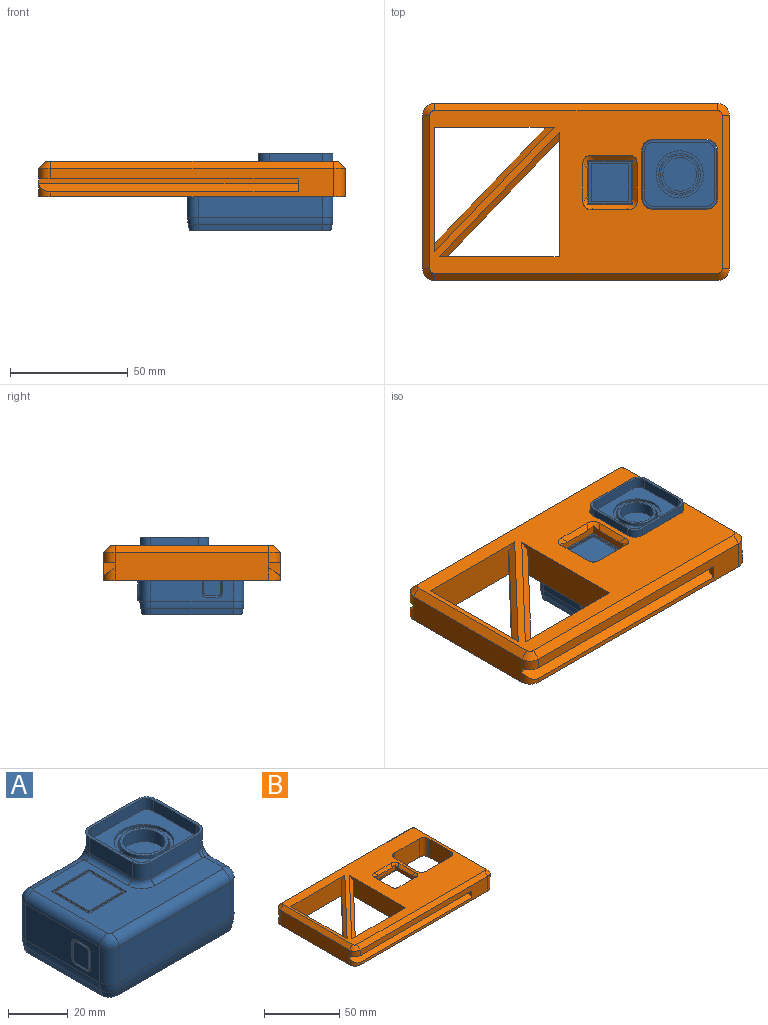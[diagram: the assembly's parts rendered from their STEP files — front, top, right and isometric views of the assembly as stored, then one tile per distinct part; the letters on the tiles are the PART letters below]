
ASSEMBLY  parts=2 mates=1
PART A: 128 faces, bbox 66x48.4x32.7 mm
  f0: plane 35.1x14.78mm, normal (-1,0,0), area 431.7mm2, adj f6,f7,f25,f94,f120,f121,f122,f123
  f1: plane 35.1x27.03mm, normal (1,0,0), area 775.9mm2, adj f4,f5,f9,f14,f20,f21,f102
  f2: plane 52.7x27.03mm, normal (0,1,0), area 881.6mm2, adj f5,f6,f10,f14,f27,f28,f57,f58
  f3: plane 52.7x14.78mm, normal (0,-1,0), area 779.1mm2, adj f4,f7,f23,f98
  f4: cylinder r=4.5mm len=14.78mm, axis (0,0,1), area 104.5mm2, adj f1,f3,f22,f100
  f5: cylinder r=4.5mm len=27.03mm, axis (0,0,1), area 191.1mm2, adj f1,f2,f14,f101
  f6: cylinder r=4.5mm len=14.78mm, axis (0,0,1), area 104.5mm2, adj f0,f2,f26,f92
  f7: cylinder r=4.5mm len=14.78mm, axis (0,0,1), area 104.5mm2, adj f0,f3,f24,f96
  f8: plane 54.3x36.7mm, normal (0,0,1), area 852.6mm2, adj f15,f16,f17,f18,f19,f21,f22,f23
  f9: cylinder r=4.5mm len=6.45mm, axis (0,0,-1), area 45.6mm2, adj f1,f13,f14,f15
  f10: cylinder r=4.5mm len=6.45mm, axis (0,0,-1), area 45.6mm2, adj f2,f11,f14,f19
  f11: plane 20.15x6.45mm, normal (-1,0,0), area 130mm2, adj f10,f12,f14,f18
  f12: cylinder r=4.5mm len=6.45mm, axis (0,0,-1), area 45.6mm2, adj f11,f13,f14,f17
  f13: plane 22.55x6.45mm, normal (0,-1,0), area 145.4mm2, adj f9,f12,f14,f16
  f14: plane 31.55x29.15mm, normal (0,0,1), area 110.5mm2, adj f1,f2,f5,f9,f10,f11,f12,f13
  f15: torus R=6.6mm, axis (0,0,1), area 7.9mm2, adj f8,f9,f16,f20
  f16: cylinder r=2.1mm len=22.55mm, axis (1,0,0), area 74.4mm2, adj f8,f13,f15,f17
  f17: torus R=6.6mm, axis (0,0,1), area 27.3mm2, adj f8,f12,f16,f18
  f18: cylinder r=2.1mm len=20.15mm, axis (0,-1,0), area 66.5mm2, adj f8,f11,f17,f19
  f19: torus R=6.6mm, axis (0,0,1), area 7.9mm2, adj f8,f10,f18,f28
  f20: bspline ~7.66x5.8mm, area 27.6mm2, adj f1,f15,f21
  f21: cylinder r=3.7mm len=8.4mm, axis (0,1,0), area 48.8mm2, adj f1,f8,f20,f22
  f22: torus R=0.8mm, axis (0,0,1), area 28.8mm2, adj f4,f8,f21,f23
  f23: cylinder r=3.7mm len=52.7mm, axis (1,0,0), area 306.3mm2, adj f3,f8,f22,f24
  f24: torus R=0.8mm, axis (0,0,1), area 28.8mm2, adj f7,f8,f23,f25
  f25: cylinder r=3.7mm len=35.1mm, axis (0,-1,0), area 204mm2, adj f0,f8,f24,f26
  f26: torus R=0.8mm, axis (0,0,1), area 28.8mm2, adj f6,f8,f25,f27
  f27: cylinder r=3.7mm len=23.6mm, axis (-1,0,0), area 137.2mm2, adj f2,f8,f26,f28
  f28: bspline ~7.66x5.8mm, area 27.6mm2, adj f2,f19,f27
  f29: plane 16x0.5mm, normal (-1,0,0), area 8mm2, adj f30,f36,f37,f38
  f30: plane 16x0.5mm, normal (0,1,0), area 8mm2, adj f29,f31,f37,f38
  f31: plane 16x0.5mm, normal (1,0,0), area 8mm2, adj f30,f36,f37,f38
  f32: plane 18x0.5mm, normal (-1,0,0), area 9mm2, adj f8,f33,f35,f37
  f33: plane 18x0.5mm, normal (0,-1,0), area 9mm2, adj f8,f32,f34,f37
  f34: plane 18x0.5mm, normal (1,0,0), area 9mm2, adj f8,f33,f35,f37
  f35: plane 18x0.5mm, normal (0,1,0), area 9mm2, adj f8,f32,f34,f37
  f36: plane 16x0.5mm, normal (0,-1,0), area 8mm2, adj f29,f31,f37,f38
  f37: plane 18x18mm, normal (0,0,1), area 68mm2, adj f29,f30,f31,f32,f33,f34,f35,f36
  f38: plane 16x16mm, normal (0,0,1), area 256mm2, adj f29,f30,f31,f36
  f39: cylinder r=1.5mm len=1.5mm, axis (0,-1,0), area 2.4mm2, adj f40,f46,f47,f105
  f40: plane 7.2x1mm, normal (0,0,1), area 7.2mm2, adj f39,f41,f47,f103
  f41: cylinder r=1.5mm len=1.5mm, axis (0,-1,0), area 2.4mm2, adj f40,f42,f47,f104
  f42: plane 7.2x1mm, normal (-1,0,0), area 7.2mm2, adj f41,f43,f47,f106
  f43: cylinder r=1.5mm len=1.5mm, axis (0,-1,0), area 2.4mm2, adj f42,f44,f47,f108
  f44: plane 7.2x1mm, normal (0,0,-1), area 7.2mm2, adj f43,f45,f47,f110
  f45: cylinder r=1.5mm len=1.5mm, axis (0,-1,0), area 2.4mm2, adj f44,f46,f47,f109
  f46: plane 7.2x1mm, normal (1,0,0), area 7.2mm2, adj f39,f45,f47,f107
  f47: plane 12.2x12.2mm, normal (0,1,0), area 41.4mm2, adj f39,f40,f41,f42,f43,f44,f45,f46
  f48: plane 7.2x0.5mm, normal (0,0,-1), area 3.6mm2, adj f49,f55,f56,f103
  f49: cylinder r=1mm len=1mm, axis (0,-1,0), area 0.8mm2, adj f48,f50,f56,f105
  f50: plane 7.2x0.5mm, normal (-1,0,0), area 3.6mm2, adj f49,f51,f56,f107
  f51: cylinder r=1mm len=1mm, axis (0,-1,0), area 0.8mm2, adj f50,f52,f56,f109
  f52: plane 7.2x0.5mm, normal (0,0,1), area 3.6mm2, adj f51,f53,f56,f110
  f53: cylinder r=1mm len=1mm, axis (0,-1,0), area 0.8mm2, adj f52,f54,f56,f108
  f54: plane 7.2x0.5mm, normal (1,0,0), area 3.6mm2, adj f53,f55,f56,f106
  f55: cylinder r=1mm len=1mm, axis (0,-1,0), area 0.8mm2, adj f48,f54,f56,f104
  f56: plane 9.2x9.2mm, normal (0,1,0), area 83.8mm2, adj f48,f49,f50,f51,f52,f53,f54,f55
  f57: cylinder r=1mm len=7.2mm, axis (1,0,0), area 11.3mm2, adj f2,f47,f58,f59
  f58: torus R=3.5mm, axis (0,1,0), area 7.1mm2, adj f2,f47,f57,f60
  f59: torus R=3.5mm, axis (0,1,0), area 7.1mm2, adj f2,f47,f57,f61
  f60: cylinder r=1mm len=7.2mm, axis (0,0,-1), area 11.3mm2, adj f2,f47,f58,f62
  f61: cylinder r=1mm len=7.2mm, axis (0,0,1), area 11.3mm2, adj f2,f47,f59,f63
  f62: torus R=3.5mm, axis (0,1,0), area 7mm2, adj f2,f47,f60,f64,f97
  f63: torus R=3.5mm, axis (0,1,0), area 7mm2, adj f2,f47,f61,f64,f93
  f64: cylinder r=1mm len=7.2mm, axis (-1,0,0), area 10.9mm2, adj f47,f62,f63,f95
  f65: plane 22.55x4.6mm, normal (0,-1,0), area 103.7mm2, adj f14,f66,f72,f73
  f66: cylinder r=3.5mm len=4.6mm, axis (0,0,1), area 25.3mm2, adj f14,f65,f67,f73
  f67: plane 20.15x4.6mm, normal (1,0,0), area 92.7mm2, adj f14,f66,f68,f73
  f68: cylinder r=3.5mm len=4.6mm, axis (0,0,1), area 25.3mm2, adj f14,f67,f69,f73
  f69: plane 22.55x4.6mm, normal (0,1,0), area 103.7mm2, adj f14,f68,f70,f73
  f70: cylinder r=3.5mm len=4.6mm, axis (0,0,1), area 25.3mm2, adj f14,f69,f71,f73
  f71: plane 20.15x4.6mm, normal (-1,0,0), area 92.7mm2, adj f14,f70,f72,f73
  f72: cylinder r=3.5mm len=4.6mm, axis (0,0,1), area 25.3mm2, adj f14,f65,f71,f73
  f73: plane 29.55x27.15mm, normal (0,0,1), area 477.6mm2, adj f65,f66,f67,f68,f69,f70,f71,f72
  f74: cylinder r=10mm len=20mm, axis (0,0,1), area 62.8mm2, adj f73,f76
  f75: cylinder r=8.8mm len=17.6mm, axis (0,0,-1), area 221.2mm2, adj f76,f77
  f76: plane 20x20mm, normal (0,0,1), area 70.9mm2, adj f74,f75
  f77: plane 17.6x17.6mm, normal (0,0,1), area 37.2mm2, adj f75,f78
  f78: cylinder r=8.1mm len=16.2mm, axis (0,0,-1), area 254.5mm2, adj f77,f79
  f79: plane 16.2x16.2mm, normal (0,0,1), area 47.8mm2, adj f78,f80
  f80: cylinder r=7.1mm len=14.2mm, axis (0,0,1), area 223.1mm2, adj f79,f81
  f81: plane 14.2x14.2mm, normal (0,0,1), area 158.4mm2, adj f80
  f82: plane 59.9x42.3mm, normal (0,0,-1), area 2522.6mm2, adj f83,f84,f85,f86,f87,f88,f89,f90
  f83: plane 52.7x2.37mm, normal (0,-0.98,-0.22), area 128.2mm2, adj f82,f84,f90,f98
  f84: cone r=4.5mm half-angle=12.7deg, axis (0,0,1), area 14.8mm2, adj f82,f83,f85,f96
  f85: plane 35.1x2.37mm, normal (-0.98,0,-0.22), area 85.4mm2, adj f82,f84,f86,f94
  f86: cone r=4.5mm half-angle=12.7deg, axis (0,0,1), area 14.8mm2, adj f82,f85,f87,f92
  f87: plane 52.7x2.47mm, normal (0,0.98,-0.22), area 129.1mm2, adj f82,f86,f88,f91,f93,f95,f97,f99
  f88: cone r=4.5mm half-angle=12.7deg, axis (0,0,1), area 14.8mm2, adj f82,f87,f89,f101
  f89: plane 35.1x2.37mm, normal (0.98,0,-0.22), area 85.4mm2, adj f82,f88,f90,f102
  f90: cone r=4.5mm half-angle=12.7deg, axis (0,0,1), area 14.8mm2, adj f82,f83,f89,f100
  f91: cylinder r=15mm len=3.33mm, axis (1,0,0), area 11mm2, adj f2,f87,f92,f93
  f92: revolved ~4.5x4.5mm, area 22.8mm2, adj f6,f86,f91,f94
  f93: bspline ~3.39x2.91mm, area 6mm2, adj f63,f87,f91,f95
  f94: cylinder r=15mm len=35.1mm, axis (0,-1,0), area 116.5mm2, adj f0,f85,f92,f96
  f95: cylinder r=15mm len=7.2mm, axis (-1,0,0), area 18.5mm2, adj f64,f87,f93,f97
  f96: revolved ~4.5x4.5mm, area 22.8mm2, adj f7,f84,f94,f98
  f97: bspline ~3.55x2.87mm, area 6mm2, adj f62,f87,f95,f99
  f98: cylinder r=15mm len=52.7mm, axis (1,0,0), area 174.9mm2, adj f3,f83,f96,f100
  f99: cylinder r=15mm len=37.93mm, axis (1,0,0), area 125.9mm2, adj f2,f87,f97,f101
  f100: revolved ~4.5x4.5mm, area 22.8mm2, adj f4,f90,f98,f102
  f101: revolved ~4.5x4.5mm, area 22.8mm2, adj f5,f88,f99,f102
  f102: cylinder r=15mm len=35.1mm, axis (0,-1,0), area 116.5mm2, adj f1,f89,f100,f101
  f103: cylinder r=0.5mm len=7.2mm, axis (-1,0,0), area 5.7mm2, adj f40,f48,f104,f105
  f104: torus R=1.5mm, axis (0,1,0), area 1.5mm2, adj f41,f55,f103,f106
  f105: torus R=1.5mm, axis (0,1,0), area 1.5mm2, adj f39,f49,f103,f107
  f106: cylinder r=0.5mm len=7.2mm, axis (0,0,-1), area 5.7mm2, adj f42,f54,f104,f108
  f107: cylinder r=0.5mm len=7.2mm, axis (0,0,1), area 5.7mm2, adj f46,f50,f105,f109
  f108: torus R=1.5mm, axis (0,1,0), area 1.5mm2, adj f43,f53,f106,f110
  f109: torus R=1.5mm, axis (0,1,0), area 1.5mm2, adj f45,f51,f107,f110
  f110: cylinder r=0.5mm len=7.2mm, axis (1,0,0), area 5.7mm2, adj f44,f52,f108,f109
  f111: cylinder r=1.2mm len=1.2mm, axis (-1,0,0), area 1.5mm2, adj f112,f118,f119,f122
  f112: plane 6.3x0.8mm, normal (0,1,0), area 5mm2, adj f111,f113,f119,f120
  f113: cylinder r=1.2mm len=1.2mm, axis (-1,0,0), area 1.5mm2, adj f112,f114,f119,f121
  f114: plane 4.8x0.8mm, normal (0,0,1), area 3.8mm2, adj f113,f115,f119,f123
  f115: cylinder r=1.2mm len=1.2mm, axis (-1,0,0), area 1.5mm2, adj f114,f116,f119,f125
  f116: plane 6.3x0.8mm, normal (0,-1,0), area 5mm2, adj f115,f117,f119,f127
  f117: cylinder r=1.2mm len=1.2mm, axis (-1,0,0), area 1.5mm2, adj f116,f118,f119,f126
  f118: plane 4.8x0.8mm, normal (0,0,-1), area 3.8mm2, adj f111,f117,f119,f124
  f119: plane 8.7x7.2mm, normal (-1,0,0), area 61.4mm2, adj f111,f112,f113,f114,f115,f116,f117,f118
  f120: plane 6.3x0.8mm, normal (-0.71,-0.71,0), area 7.1mm2, adj f0,f112,f121,f122
  f121: cone r=1.2mm half-angle=45deg, axis (-1,0,0), area 2.8mm2, adj f0,f113,f120,f123
  f122: cone r=1.2mm half-angle=45deg, axis (-1,0,0), area 2.8mm2, adj f0,f111,f120,f124
  f123: plane 4.8x0.8mm, normal (-0.71,0,-0.71), area 5.4mm2, adj f0,f114,f121,f125
  f124: plane 4.8x0.8mm, normal (-0.71,0,0.71), area 5.4mm2, adj f0,f118,f122,f126
  f125: cone r=1.2mm half-angle=45deg, axis (-1,0,0), area 2.8mm2, adj f0,f115,f123,f127
  f126: cone r=1.2mm half-angle=45deg, axis (-1,0,0), area 2.8mm2, adj f0,f117,f124,f127
  f127: plane 6.3x0.8mm, normal (-0.71,0.71,0), area 7.1mm2, adj f0,f116,f125,f126
PART B: 75 faces, bbox 130x75x15.5 mm
  f0: plane 124x69mm, normal (0,0,1), area 4420.2mm2, adj f12,f13,f14,f15,f16,f17,f18,f19
  f1: plane 130x75mm, normal (0,0,-1), area 4263.1mm2, adj f3,f5,f7,f8,f9,f10,f11,f12
  f2: plane 62.2x46.51mm, normal (0,0,-1), area 1359.1mm2, adj f12,f18,f21,f22,f23,f24,f25,f26
  f3: cylinder r=5mm len=5.5mm, axis (0,0,-1), area 25.7mm2, adj f1,f5,f7,f32
  f4: cylinder r=5mm len=5mm, axis (0,0,-1), area 35.3mm2, adj f5,f7,f33,f38
  f5: plane 120x12mm, normal (0,-1,0), area 862.4mm2, adj f1,f3,f4,f8,f32,f33,f35,f36
  f6: cylinder r=5mm len=5mm, axis (0,0,-1), area 35.3mm2, adj f7,f11,f28,f42
  f7: plane 65x12mm, normal (-1,0,0), area 780mm2, adj f1,f3,f4,f6,f20,f30,f34,f40
  f8: cylinder r=5mm len=12mm, axis (0,0,-1), area 94.2mm2, adj f1,f5,f9,f37
  f9: plane 65x12mm, normal (1,0,0), area 780mm2, adj f1,f8,f10,f39
  f10: cylinder r=5mm len=12mm, axis (0,0,-1), area 94.2mm2, adj f1,f9,f11,f41
  f11: plane 120x12mm, normal (0,1,0), area 862.4mm2, adj f1,f6,f10,f20,f28,f29,f31,f43
  f12: plane 35.6x15mm, normal (-1,0,0), area 463mm2, adj f0,f1,f2,f13,f19,f21,f48
  f13: cylinder r=4.5mm len=4.5mm, axis (0,0,-1), area 20.5mm2, adj f0,f12,f14,f48
  f14: plane 23.05x2.9mm, normal (0,1,0), area 66.8mm2, adj f0,f13,f15,f47
  f15: cylinder r=4.5mm len=4.5mm, axis (0,0,-1), area 20.5mm2, adj f0,f14,f16,f46
  f16: plane 20.65x2.9mm, normal (1,0,0), area 59.9mm2, adj f0,f15,f17,f45
  f17: cylinder r=4.5mm len=4.5mm, axis (0,0,-1), area 20.5mm2, adj f0,f16,f18,f44
  f18: plane 35.44x15mm, normal (0,-1,0), area 473.4mm2, adj f0,f1,f2,f17,f19,f44,f51
  f19: cylinder r=4.5mm len=15mm, axis (0,0,-1), area 106mm2, adj f0,f1,f12,f18
  f20: cylinder r=5mm len=5.5mm, axis (0,0,-1), area 25.7mm2, adj f1,f7,f11,f29
  f21: cylinder r=4.5mm len=10mm, axis (0,0,1), area 70.7mm2, adj f1,f2,f12,f22
  f22: plane 53.2x10mm, normal (0,1,0), area 532mm2, adj f1,f2,f21,f23
  f23: cylinder r=4.5mm len=10mm, axis (0,0,1), area 70.7mm2, adj f1,f2,f22,f24
  f24: plane 35.6x10mm, normal (1,0,0), area 356mm2, adj f1,f2,f23,f25
  f25: cylinder r=4.5mm len=10mm, axis (0,0,1), area 70.7mm2, adj f1,f2,f24,f26
  f26: plane 10x0.74mm, normal (0,-1,0), area 7.4mm2, adj f1,f2,f25,f50
  f27: plane 13.19x10mm, normal (0,-1,0), area 131.9mm2, adj f1,f2,f49,f52
  f28: plane 110x5mm, normal (0,0,-1), area 544.6mm2, adj f6,f11,f30,f31
  f29: plane 110x5mm, normal (0,0.57,0.82), area 664.9mm2, adj f11,f20,f30,f31
  f30: plane 110x2mm, normal (0,1,0), area 220mm2, adj f7,f28,f29,f31
  f31: plane 5.5x5mm, normal (-1,0,0), area 18.8mm2, adj f11,f28,f29,f30
  f32: plane 110x5mm, normal (0,-0.57,0.82), area 664.9mm2, adj f3,f5,f34,f35
  f33: plane 110x5mm, normal (0,0,-1), area 544.6mm2, adj f4,f5,f34,f35
  f34: plane 110x2mm, normal (0,-1,0), area 220mm2, adj f7,f32,f33,f35
  f35: plane 5.5x5mm, normal (-1,0,0), area 18.8mm2, adj f5,f32,f33,f34
  f36: plane 120x3mm, normal (0,-0.71,0.71), area 509.1mm2, adj f0,f5,f37,f38
  f37: cone r=2mm half-angle=45deg, axis (0,0,-1), area 23.3mm2, adj f0,f8,f36,f39
  f38: cone r=2mm half-angle=45deg, axis (0,0,-1), area 23.3mm2, adj f0,f4,f36,f40
  f39: plane 65x3mm, normal (0.71,0,0.71), area 275.8mm2, adj f0,f9,f37,f41
  f40: plane 65x3mm, normal (-0.71,0,0.71), area 275.8mm2, adj f0,f7,f38,f42
  f41: cone r=2mm half-angle=45deg, axis (0,0,-1), area 23.3mm2, adj f0,f10,f39,f43
  f42: cone r=2mm half-angle=45deg, axis (0,0,-1), area 23.3mm2, adj f0,f6,f40,f43
  f43: plane 120x3mm, normal (0,0.71,0.71), area 509.1mm2, adj f0,f11,f41,f42
  f44: torus R=6.6mm, axis (0,0,1), area 18.7mm2, adj f2,f17,f18,f45
  f45: cylinder r=2.1mm len=20.65mm, axis (0,1,0), area 68.1mm2, adj f2,f16,f44,f46
  f46: torus R=6.6mm, axis (0,0,1), area 27.3mm2, adj f2,f15,f45,f47
  f47: cylinder r=2.1mm len=23.05mm, axis (-1,0,0), area 76mm2, adj f2,f14,f46,f48
  f48: torus R=6.6mm, axis (0,0,1), area 18.7mm2, adj f2,f12,f13,f47
  f49: cylinder r=0.96mm len=10mm, axis (0,0,-1), area 15mm2, adj f1,f2,f27,f50
  f50: cylinder r=0.96mm len=10mm, axis (0,0,-1), area 15mm2, adj f1,f2,f26,f49
  f51: cylinder r=0.96mm len=10mm, axis (0,0,-1), area 15mm2, adj f1,f2,f18,f52
  f52: cylinder r=0.96mm len=10mm, axis (0,0,1), area 15mm2, adj f1,f2,f27,f51
  f53: plane 19x3.95mm, normal (0,1,0), area 59.3mm2, adj f2,f54,f56,f60,f63,f64
  f54: plane 19x3.95mm, normal (-1,0,0), area 59.3mm2, adj f2,f53,f55,f58,f61,f63
  f55: plane 19x3.95mm, normal (0,-1,0), area 59.3mm2, adj f2,f54,f56,f57,f61,f62
  f56: plane 19x3.95mm, normal (1,0,0), area 59.3mm2, adj f2,f53,f55,f59,f62,f64
  f57: plane 15.93x2mm, normal (0,-0.71,0.71), area 39.4mm2, adj f0,f55,f61,f62
  f58: plane 15.93x2mm, normal (-0.71,0,0.71), area 39.4mm2, adj f0,f54,f61,f63
  f59: plane 15.93x2mm, normal (0.71,0,0.71), area 39.4mm2, adj f0,f56,f62,f64
  f60: plane 15.93x2mm, normal (0,0.71,0.71), area 39.4mm2, adj f0,f53,f63,f64
  f61: cylinder r=5mm len=6.08mm, axis (-0.58,-0.58,-0.58), area 15.2mm2, adj f0,f54,f55,f57,f58
  f62: cylinder r=5mm len=6.08mm, axis (0.58,-0.58,-0.58), area 15.2mm2, adj f0,f55,f56,f57,f59
  f63: cylinder r=5mm len=6.08mm, axis (0.58,-0.58,0.58), area 15.2mm2, adj f0,f53,f54,f58,f60
  f64: cylinder r=5mm len=6.08mm, axis (-0.58,-0.58,0.58), area 15.2mm2, adj f0,f53,f56,f59,f60
  f65: plane 49.22x47.26mm, normal (0.72,-0.69,0), area 682.4mm2, adj f66,f67,f71,f73
  f66: plane 52.83x15mm, normal (-1,0,0), area 747.4mm2, adj f0,f1,f65,f67,f71,f73
  f67: plane 50.72x15mm, normal (0,1,0), area 717.5mm2, adj f0,f1,f65,f66,f71,f73
  f68: plane 52.83x15mm, normal (1,0,0), area 747.4mm2, adj f0,f1,f69,f70,f72,f74
  f69: plane 50.72x15mm, normal (0,-1,0), area 717.5mm2, adj f0,f1,f68,f70,f72,f74
  f70: plane 49.22x47.26mm, normal (-0.72,0.69,0), area 682.4mm2, adj f68,f69,f72,f74
  f71: plane 52.83x50.72mm, normal (0.51,-0.49,0.71), area 250.1mm2, adj f0,f65,f66,f67
  f72: plane 52.83x50.72mm, normal (-0.51,0.49,0.71), area 250.1mm2, adj f0,f68,f69,f70
  f73: plane 52.83x50.72mm, normal (0.51,-0.49,-0.71), area 250.1mm2, adj f1,f65,f66,f67
  f74: plane 52.83x50.72mm, normal (-0.51,0.49,-0.71), area 250.1mm2, adj f1,f68,f69,f70
PLACE A t=(93.9,0,9.75)mm
PLACE B t=(93.9,0,10)mm
MATE slider B.f0 <-> A.f74  axis (0,0,1) through (108.98,7.47,15)mm
